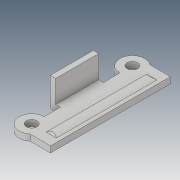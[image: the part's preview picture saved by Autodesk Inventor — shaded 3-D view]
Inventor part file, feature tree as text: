
AUTODESK INVENTOR PART (.ipt)
format: ipt  version: 2019 (Build 230136000, 136)  size: 140,800 bytes
history: native  units: mm
features: extrude x4, sketch x3, fillet x1
ambient origin geometry x8: Origin, YZ Plane, XZ Plane, XY Plane, X Axis, Y Axis, Z Axis, Center Point
bodies: Solid1 (feature_tree)
feature tree (8):
  extrude  "Extrusion1"  Depth=2.2mm
  extrude  "Extrusion2"  Depth=2.0mm
  fillet  "Fillet1"  Radius=2.0mm
  sketch  "Sketch3"  dims[d7=0.0mm d10=1.3mm d11=0.0mm d13=0.5mm d14=0.0mm d15=2.0mm d17=2.0mm d18=2.0mm d19=21.0mm d20=0.8mm d25=6.0mm d26=0.0mm d27=1.5mm d28=1.5mm d29=3.0mm d30=8.0mm d31=8.0mm d32=3.5mm d33=0.0mm]
  extrude  "Extrusion3"  Depth=1.3mm TaperAngle=0.0deg
  extrude  "Extrusion4"  Depth=6.0mm TaperAngle=0.0deg
  sketch  "Sketch1"  dims[d0=25.0mm d2=2.2mm]
  sketch  "Sketch2"  dims[d3=2.2mm d4=2.0mm d5=0.0mm d6=2.0mm]
